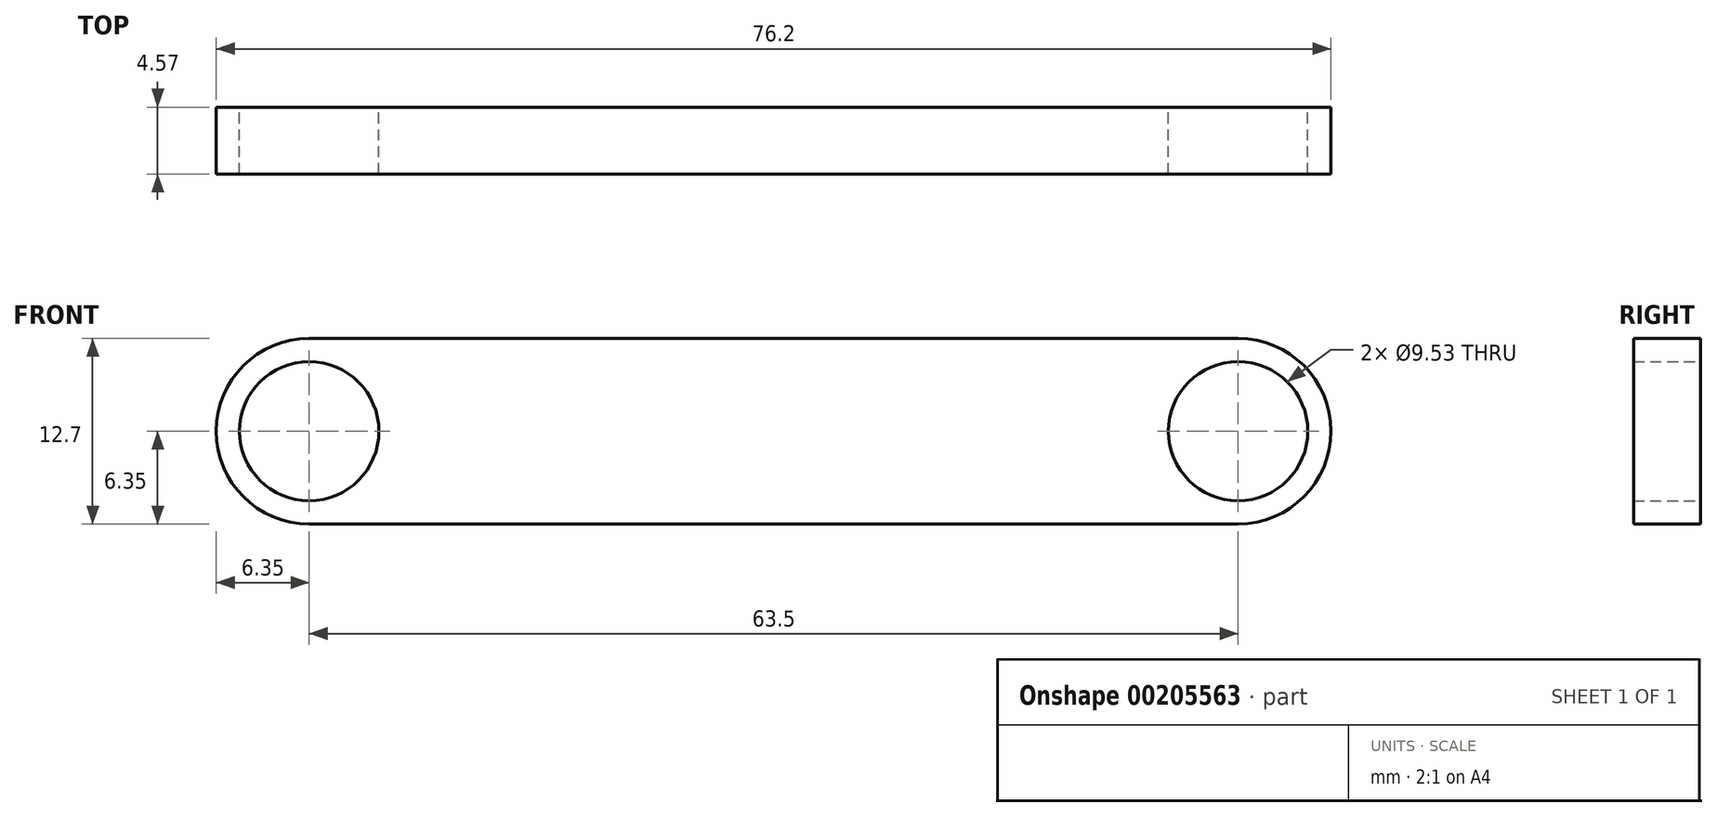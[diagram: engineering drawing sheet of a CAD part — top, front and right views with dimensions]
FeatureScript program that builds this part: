
annotation { "Feature Type Name" : "Feature", "Feature Type Description" : "" }
export const myFeature = defineFeature(function(context is Context, id is Id, definition is map)
    precondition{}
    {
        {
            var Q0;
            Q0=qCreatedBy(makeId("Front.planeOp"),FACE);
            var sketch = newSketch(context, id + "F0", { "sketchPlane" : qUnion([Q0])});
            skCircle(sketch, "E0", {"center": v(-31.75, 0) * mm, "radius": 4.76 * mm});
            skCircle(sketch, "E1", {"center": v(31.75, 0) * mm, "radius": 4.76 * mm});
            skCircle(sketch, "E2", {"center": v(-31.75, 0) * mm, "radius": 6.35 * mm});
            skCircle(sketch, "E3", {"center": v(31.75, 0) * mm, "radius": 6.35 * mm});
            skLineSegment(sketch, "E4", {"start": v(-31.75, 6.35) * mm, "end": v(31.75, 6.35) * mm});
            skLineSegment(sketch, "E5", {"start": v(-31.75, -6.35) * mm, "end": v(31.75, -6.35) * mm});
            skSolve(sketch);
        }
        {
            var Q0;
            Q0=qSketchRegion(id+"F0",true);
            extrude(context, id + "F1", {"entities" : qUnion([Q0]), "flatOperationType" : FlatOperationType.REMOVE, "offsetDistance" : 25.4 * mm, "depth" : 4.57 * mm, "domain" : OperationDomain.MODEL});
        }
    });
